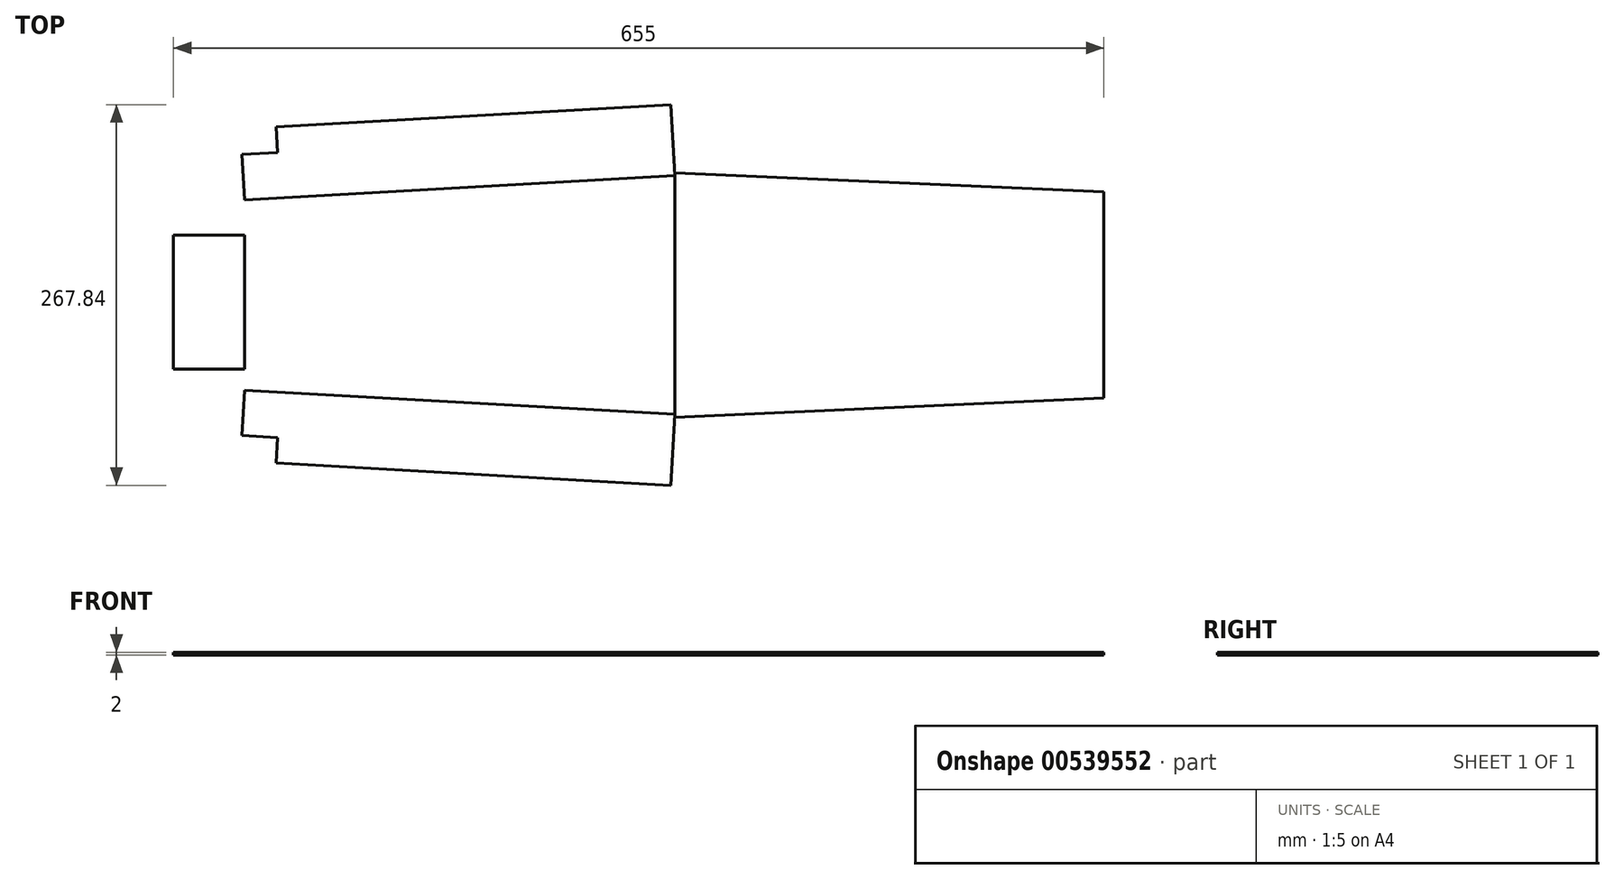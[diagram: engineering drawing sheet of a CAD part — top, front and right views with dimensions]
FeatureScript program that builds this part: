
annotation { "Feature Type Name" : "Feature", "Feature Type Description" : "" }
export const myFeature = defineFeature(function(context is Context, id is Id, definition is map)
    precondition{}
    {
        {
            var Q0;
            Q0=qCreatedBy(makeId("Top.planeOp"),FACE);
            var sketch = newSketch(context, id + "F0", { "sketchPlane" : qUnion([Q0])});
            skLineSegment(sketch, "E0", {"start": v(0, 0) * mm, "end": v(-303, 0) * mm, "construction": true});
            skLineSegment(sketch, "E1", {"start": v(0, 0) * mm, "end": v(275, 0) * mm, "construction": true});
            skLineSegment(sketch, "E2", {"start": v(-303, 0) * mm, "end": v(-353, 0) * mm, "construction": true});
            skLineSegment(sketch, "E3", {"start": v(275, 0) * mm, "end": v(302, 0) * mm, "construction": true});
            skLineSegment(sketch, "E4", {"start": v(0, 0) * mm, "end": v(0, 86) * mm});
            skLineSegment(sketch, "E5", {"start": v(302, 0) * mm, "end": v(302, 72.5) * mm});
            skLineSegment(sketch, "E6", {"start": v(302, 72.5) * mm, "end": v(0, 86) * mm});
            skLineSegment(sketch, "E7", {"start": v(275, 0) * mm, "end": v(275, 73.7) * mm});
            skLineSegment(sketch, "E8", {"start": v(-303, 0) * mm, "end": v(-303, 67) * mm});
            skLineSegment(sketch, "E9", {"start": v(0, 0) * mm, "end": v(0, 84) * mm});
            skPoint(sketch, "E9.endSnap0", {"position": v(0, 43) * mm});
            skLineSegment(sketch, "E10", {"start": v(0, 84) * mm, "end": v(-303, 67) * mm});
            skLineSegment(sketch, "E11", {"start": v(0, 84) * mm, "end": v(-2.8, 133.92) * mm});
            skLineSegment(sketch, "E12", {"start": v(-2.8, 133.92) * mm, "end": v(-280.73, 118.33) * mm});
            skLineSegment(sketch, "E13", {"start": v(-303, 67) * mm, "end": v(-304.8, 98.95) * mm});
            skLineSegment(sketch, "E14", {"start": v(-304.8, 98.95) * mm, "end": v(-279.83, 100.35) * mm});
            skLineSegment(sketch, "E15", {"start": v(-279.83, 100.35) * mm, "end": v(-280.73, 118.33) * mm});
            skLineSegment(sketch, "E16.MirrorCS", {"start": v(-303, 0) * mm, "end": v(-303, -67) * mm});
            skLineSegment(sketch, "E17.MirrorCS", {"start": v(-303, -67) * mm, "end": v(-304.8, -98.95) * mm});
            skLineSegment(sketch, "E18.MirrorCS", {"start": v(-304.8, -98.95) * mm, "end": v(-279.83, -100.35) * mm});
            skLineSegment(sketch, "E19.MirrorCS", {"start": v(-279.83, -100.35) * mm, "end": v(-280.73, -118.33) * mm});
            skLineSegment(sketch, "E20.MirrorCS", {"start": v(-2.8, -133.92) * mm, "end": v(-280.73, -118.33) * mm});
            skLineSegment(sketch, "E21.MirrorCS", {"start": v(0, -84) * mm, "end": v(-2.8, -133.92) * mm});
            skLineSegment(sketch, "E22.MirrorCS", {"start": v(0, -84) * mm, "end": v(-303, -67) * mm});
            skLineSegment(sketch, "E23.MirrorCS", {"start": v(0, 0) * mm, "end": v(0, -84) * mm});
            skLineSegment(sketch, "E24.MirrorCS", {"start": v(302, -72.5) * mm, "end": v(0, -86) * mm});
            skLineSegment(sketch, "E25.MirrorCS", {"start": v(275, 0) * mm, "end": v(275, -73.7) * mm});
            skLineSegment(sketch, "E26.MirrorCS", {"start": v(302, 0) * mm, "end": v(302, -72.5) * mm});
            skLineSegment(sketch, "E27", {"start": v(-353, 0) * mm, "end": v(-353, 42) * mm});
            skLineSegment(sketch, "E28", {"start": v(-353, 42) * mm, "end": v(-303, 42) * mm});
            skLineSegment(sketch, "E29", {"start": v(-353, 0) * mm, "end": v(-353, -52) * mm});
            skLineSegment(sketch, "E30", {"start": v(-353, -52) * mm, "end": v(-303, -52) * mm});
            skText(sketch, "E31", { "text": "Lamiera 2mm\n", "fontName": "OpenSans-Regular.ttf"});
            skLineSegment(sketch, "E32", {"start": v(0, -84) * mm, "end": v(0, -86) * mm});
            const initialGuessF0  = {"E31": [-0.2023, 0.17552, 1, 0, 0.01498]};
            skSetInitialGuess(sketch, initialGuessF0);
            skSolve(sketch);
        }
        {
            var Q0;
            {var subQ3=sQuery(id+"F0.wireOp",EDGE,"E5");Q0=makeQuery(id+"F0.imprint","IMPRINT",FACE,{"disambiguationData":[TD([[makeQuery(id+"F0.imprint","IMPRINT",EDGE,{"derivedFrom":subQ3}),1.0]])]});}
            var Q1;
            {var subQ2=sQuery(id+"F0.wireOp",EDGE,"E4");Q1=makeQuery(id+"F0.imprint","IMPRINT",FACE,{"disambiguationData":[TD([[makeQuery(id+"F0.imprint","IMPRINT",EDGE,{"derivedFrom":subQ2}),-1.0]])]});}
            var Q2;
            Q2=makeQuery(id+"F0.imprint","IMPRINT",FACE,{"disambiguationData":[TD([[makeQuery(id+"F0.imprint","IMPRINT",EDGE,{"derivedFrom":sQuery(id+"F0.wireOp",EDGE,"E9")}),1.0]])]});
            var Q3;
            Q3=makeQuery(id+"F0.imprint","IMPRINT",FACE,{"disambiguationData":[TD([[makeQuery(id+"F0.imprint","IMPRINT",EDGE,{"derivedFrom":sQuery(id+"F0.wireOp",EDGE,"E17.MirrorCS")}),1.0]])]});
            var Q4;
            Q4=makeQuery(id+"F0.imprint","IMPRINT",FACE,{"disambiguationData":[TD([[makeQuery(id+"F0.imprint","IMPRINT",EDGE,{"derivedFrom":sQuery(id+"F0.wireOp",EDGE,"E10")}),-1.0]])]});
            var Q5;
            Q5=makeQuery(id+"F0.imprint","IMPRINT",FACE,{"disambiguationData":[TD([[makeQuery(id+"F0.imprint","IMPRINT",EDGE,{"derivedFrom":sQuery(id+"F0.wireOp",EDGE,"E27")}),-1.0]])]});
            extrude(context, id + "F1", {"entities" : qUnion([Q0, Q1, Q2, Q3, Q4, Q5]), "depth" : 2 * mm, "offsetDistance" : 25 * mm});
        }
    });
